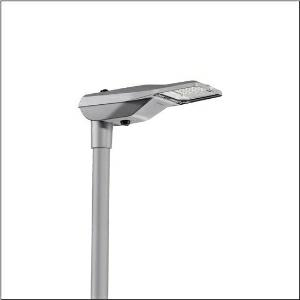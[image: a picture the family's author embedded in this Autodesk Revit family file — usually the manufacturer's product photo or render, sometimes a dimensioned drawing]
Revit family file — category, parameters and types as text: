
# Revit family: streetlight_sl_21_micro___stw1_0a_5xe1e33t08db_9129
name_source: partatom
category: Lighting Fixtures
units: mm (PartAtom-declared; Revit-internal decimal feet)

## family parameters
Cut with Voids When Loaded = No
Host = Face
Light Source = No
Part Type = Normal
Room Calculation Point = No
Round Connector Dimension = Use Diameter
Shared = No

## types (1)
- --- (1 x LED, 5110 lm, 39.1 W, 3000K)
    Apparent Load = 39 VA
    CIE Flux Codes = 38 75 98 100 100
    Color Rendering = 70
    Color Temperature = 3000K
    Default Elevation = 1800 mm
    Description = Streetlight SL 21 micro, mast luminaire, primary light control with lens, of PMMA, primary optical cover: cover, of toughened safety glass, transparent, light distribution: STW1.0a, light emission: direct distribution, primary light characteristic: asymmetric, installation type: side-entry, post-top, LED, High Power LED, rated luminous flux: 5.110lm, luminous efficacy: 131lm/W, light colour: 730, colour temperature: 3000K, control gear: D4i, control: flexible luminous flux parameterisation, time-dependent luminous flux control, constant luminous flux control, overheat protection, pre-setting: logarithmic dimming characteristic, mains connection: 220..240V, AC, 50/60Hz, start of lifetime: 39W, end of service life: 41W, reduction: 18W, luminaire housing, of diecast aluminium, powder-coated, Siteco® metallic grey (DB 702S), corrosivity category C5 mid according to DIN EN ISO 12944, please order mast flange separately, inclination adjustable: 0°, 5°, 10°, 15°, sealing non-destructively replaceable, multi-level sealing system, length: 528mm, width: 235mm, height: 110mm, mast flange for spigot size: 42mm (side-entry): 5XC10008XM4, 60/48mm (side-entry/post-top): 5XC10108XM2, 76/60mm (side-entry/post-top): 5XC10108XM1, Smart Interface below and above, protection rating (complete): IP66, insulation class (complete): insulation class II (safety insulation), certification: CE, ENEC, ENEC+, VDE, impact resistance: IK10, permissible operating ambient temperature for outdoor applications: -40..+50°C, standard-compliant lighting for roads and squares, packaging unit: 1 piece

Light Distribution: STW1.0a
    Height = 110 mm
    Lamp = 1 x LED
    Lamp Light Flux = 5110 lm
    Lamp Power = 39.1 W
    Lamp count = 1
    Length = 528 mm
    Luminous efficacy = 131 lm/W
    Manufacturer = Siteco
    ModVariant = No
    Model = 5XE1E33T08DB
    Number of Poles = 1
    OnlyDefault = Yes
    Power Factor = 1
    Product Name = Streetlight SL 21 micro | STW1.0a
    Product group = mast luminaire | pylon top
    ProductGroupID = 6100
    Protection Class = Protection class II
    Protection Degree = IP 66
    RLX_Detail_Level = 1
    RLX_Emergency_Light_Flux = 0 lm
    RLX_Emergency_Type = 0
    RLX_Emergency_Type_DB = No
    RlxData = <blob elided: 97769 chars, md5=06174d9e>
    Socket = socket
    Standby Power = 0 W
    System Light Flux = 5110 lm
    System Power = 39 W
    Type Comments = factory setting: luminous flux: 100 % | dim-lin: 254 | 765 mA
    Type Image = l_1007239.jpg
    URL = http://relux.com
    VarID = @adj_176751
    Voltage = 0 V
    Weight = 0.00 kg
    Width = 235 mm

## geometry (parser evidence)
native form markers: Blend x4, Sweep x9
no freeform markers — native parametric forms only
